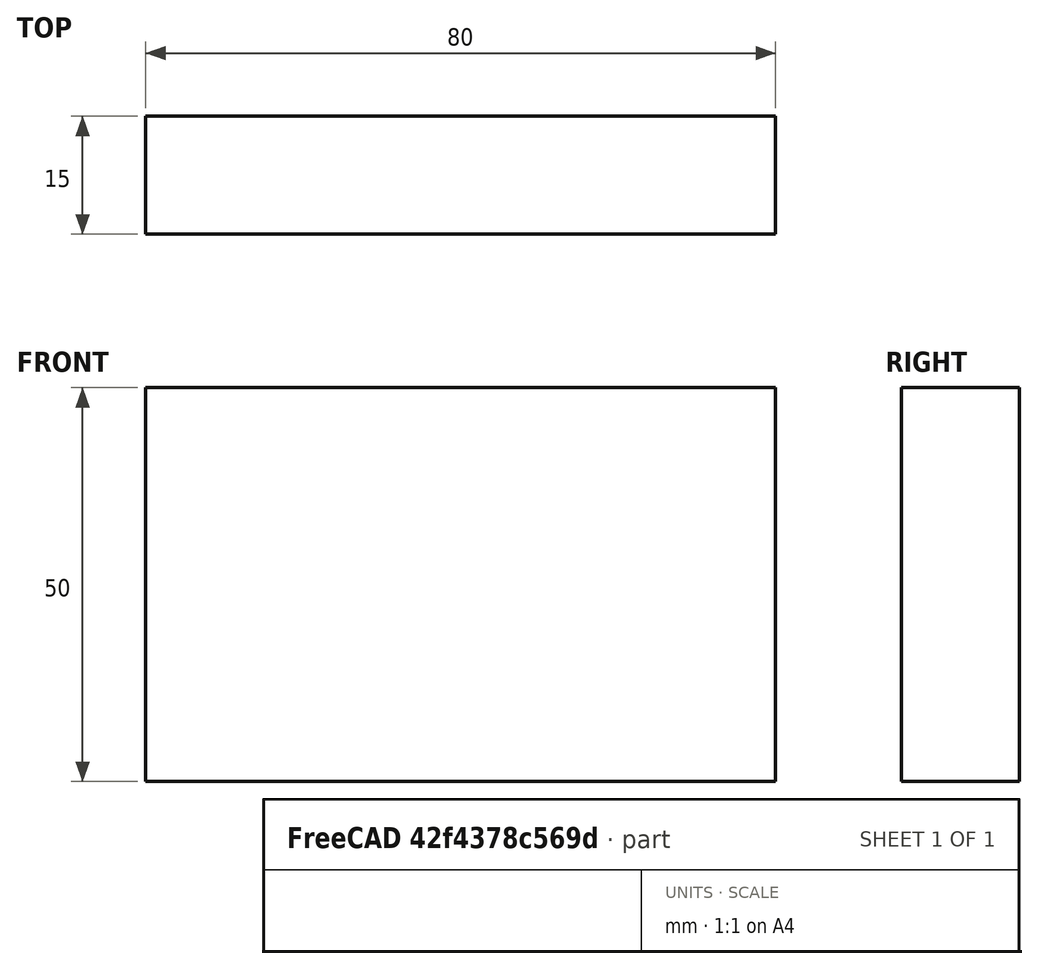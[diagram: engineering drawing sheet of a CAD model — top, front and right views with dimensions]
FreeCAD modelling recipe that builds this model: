
FCSTD DOCUMENT  (FreeCAD 0.15R4671 (Git))
Label: Flat Bar 80x15 EN10058 S235JR
License: All rights reserved
LicenseURL: http://en.wikipedia.org/wiki/All_rights_reserved
objects: Sketcher::SketchObject×1, Part::Extrusion×1
note: 2 computed .brp shape members not serialized (recipe doc carries the construction recipe); baked Part::Feature solids carry a one-line shape summary decoded from their .brp

FEATURE [Sketcher::SketchObject] Sketch
  sketch-geometry (4):
    g0: LineSegment StartX=-40 StartY=-7.5 StartZ=0 EndX=40 EndY=-7.5 EndZ=0
    g1: LineSegment StartX=40 StartY=-7.5 StartZ=0 EndX=40 EndY=7.5 EndZ=0
    g2: LineSegment StartX=40 StartY=7.5 StartZ=0 EndX=-40 EndY=7.5 EndZ=0
    g3: LineSegment StartX=-40 StartY=7.5 StartZ=0 EndX=-40 EndY=-7.5 EndZ=0
  constraints (12):
    c: Coincident(g0,g1)
    c: Coincident(g1,g2)
    c: Coincident(g2,g3)
    c: Coincident(g3,g0)
    c: Horizontal(g0)
    c: Horizontal(g2)
    c: Vertical(g1)
    c: Vertical(g3)
    c: Symmetric(g1,g2,g-2)
    c: Symmetric(g0,g1,g-1)
    c: DistanceY(g1) = 15
    c: DistanceX(g0) = 80
FEATURE [Part::Extrusion] Extrude  label="Flat Bar 80x15 EN10058 S235JR"
  Base = -> Sketch
  Dir = (0,0,50)
  Solid = true
